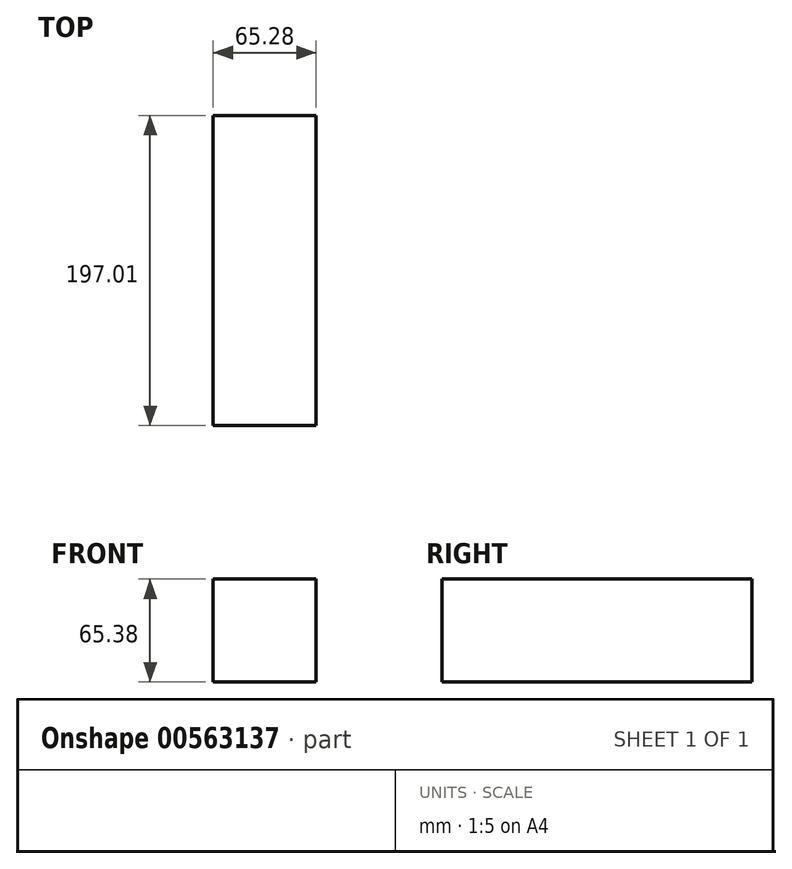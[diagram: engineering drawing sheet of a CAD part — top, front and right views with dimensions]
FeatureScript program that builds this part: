
annotation { "Feature Type Name" : "Feature", "Feature Type Description" : "" }
export const myFeature = defineFeature(function(context is Context, id is Id, definition is map)
    precondition{}
    {
        {
            var Q0;
            Q0=qCreatedBy(makeId("Front.planeOp"),FACE);
            var sketch = newSketch(context, id + "F0", { "sketchPlane" : qUnion([Q0])});
            skLineSegment(sketch, "E0.bottom", {"start": v(-65.28, 65.38) * mm, "end": v(0, 65.38) * mm});
            skLineSegment(sketch, "E0.top", {"start": v(-65.28, 0) * mm, "end": v(0, 0) * mm});
            skLineSegment(sketch, "E0.left", {"start": v(-65.28, 65.38) * mm, "end": v(-65.28, 0) * mm});
            skLineSegment(sketch, "E0.right", {"start": v(0, 65.38) * mm, "end": v(0, 0) * mm});
            skSolve(sketch);
        }
        {
            var Q0;
            Q0=makeQuery(id+"F0.imprint","IMPRINT",FACE,{"disambiguationData":[TD([[makeQuery(id+"F0.imprint","IMPRINT",EDGE,{"derivedFrom":sQuery(id+"F0.wireOp",EDGE,"E0.bottom")}),-1.0]])]});
            extrude(context, id + "F1", {"entities" : qUnion([Q0]), "depth" : 197 * mm, "offsetDistance" : 25.4 * mm});
        }
    });
